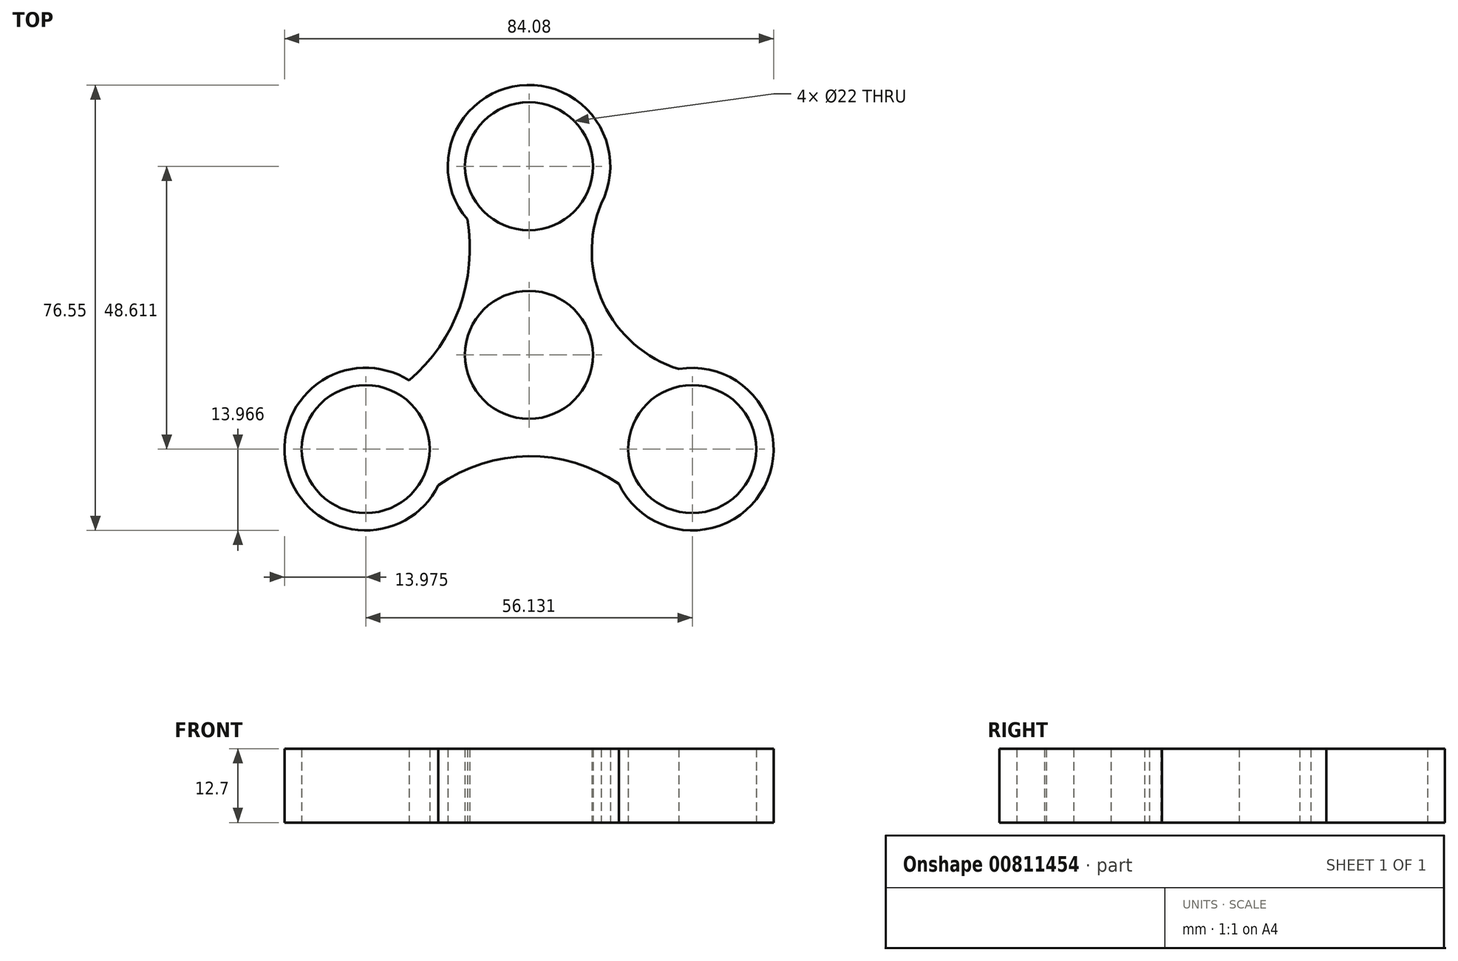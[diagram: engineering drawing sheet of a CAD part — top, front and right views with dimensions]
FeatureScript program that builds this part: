
annotation { "Feature Type Name" : "Feature", "Feature Type Description" : "" }
export const myFeature = defineFeature(function(context is Context, id is Id, definition is map)
    precondition{}
    {
        {
            var Q0;
            Q0=qCreatedBy(makeId("Top.planeOp"),FACE);
            var sketch = newSketch(context, id + "F0", { "sketchPlane" : qUnion([Q0])});
            skCircle(sketch, "E0", {"center": v(0, 0) * mm, "radius": 44.45 * mm});
            skCircle(sketch, "E1", {"center": v(0, 0) * mm, "radius": 11 * mm});
            skCircle(sketch, "E2", {"center": v(0, 32.4) * mm, "radius": 11 * mm});
            skCircle(sketch, "E3.1.0", {"center": v(-28.07, -16.2) * mm, "radius": 11 * mm});
            skCircle(sketch, "E3.2.0", {"center": v(28.07, -16.2) * mm, "radius": 11 * mm});
            skCircle(sketch, "E4", {"center": v(-28.07, -16.2) * mm, "radius": 13.97 * mm});
            skCircle(sketch, "E5", {"center": v(28.07, -16.2) * mm, "radius": 13.97 * mm});
            skCircle(sketch, "E6", {"center": v(0, 32.4) * mm, "radius": 13.97 * mm});
            skCircle(sketch, "E7", {"center": v(0, 0) * mm, "radius": 13.97 * mm});
            skArc(sketch, "E8", {"start": v(-20.59, -4.4) * mm, "mid": v(-11.95, 8.14) * mm, "end": v(-10.6, 23.3) * mm});
            skArc(sketch, "E9", {"start": v(15.42, -22.15) * mm, "mid": v(-0.12, -17.42) * mm, "end": v(-15.57, -22.45) * mm});
            skArc(sketch, "E10", {"start": v(12.4, 25.98) * mm, "mid": v(12.8, 8.83) * mm, "end": v(25.74, -2.43) * mm});
            skSolve(sketch);
        }
        {
            var Q0;
            Q0=makeQuery(id+"F0.imprint","IMPRINT",FACE,{"disambiguationData":[TD([[makeQuery(id+"F0.imprint","IMPRINT",EDGE,{"derivedFrom":sQuery(id+"F0.wireOp",EDGE,"E2")}),-1.0]])]});
            var Q1;
            Q1=makeQuery(id+"F0.imprint","IMPRINT",FACE,{"disambiguationData":[TD([[makeQuery(id+"F0.imprint","IMPRINT",EDGE,{"derivedFrom":sQuery(id+"F0.wireOp",EDGE,"E3.1.0")}),-1.0]])]});
            var Q2;
            {var subQ0=sQuery(id+"F0.wireOp",EDGE,"E4");var subQ1=sQuery(id+"F0.wireOp",EDGE,"E0");var subQ2=makeQuery(id+"F0.imprint","INTERSECT",VERTEX,{"disambiguationData":[OD(0.0)],"derivedFrom":[subQ1,subQ0]});Q2=makeQuery(id+"F0.imprint","IMPRINT",FACE,{"disambiguationData":[TD([[makeQuery(id+"F0.imprint","IMPRINT",EDGE,{"disambiguationData":[TD([[subQ2,-1.0]])],"derivedFrom":subQ1}),-1.0]])]});}
            var Q3;
            {var subQ0=sQuery(id+"F0.wireOp",EDGE,"E6");var subQ1=sQuery(id+"F0.wireOp",EDGE,"E0");var subQ2=makeQuery(id+"F0.imprint","INTERSECT",VERTEX,{"disambiguationData":[OD(0.0)],"derivedFrom":[subQ1,subQ0]});Q3=makeQuery(id+"F0.imprint","IMPRINT",FACE,{"disambiguationData":[TD([[makeQuery(id+"F0.imprint","IMPRINT",EDGE,{"disambiguationData":[TD([[subQ2,1.0]])],"derivedFrom":subQ1}),-1.0]])]});}
            var Q4;
            Q4=makeQuery(id+"F0.imprint","IMPRINT",FACE,{"disambiguationData":[TD([[makeQuery(id+"F0.imprint","IMPRINT",EDGE,{"derivedFrom":sQuery(id+"F0.wireOp",EDGE,"E3.2.0")}),-1.0]])]});
            var Q5;
            {var subQ0=sQuery(id+"F0.wireOp",EDGE,"E5");var subQ1=sQuery(id+"F0.wireOp",EDGE,"E0");var subQ2=makeQuery(id+"F0.imprint","INTERSECT",VERTEX,{"disambiguationData":[OD(0.0)],"derivedFrom":[subQ1,subQ0]});Q5=makeQuery(id+"F0.imprint","IMPRINT",FACE,{"disambiguationData":[TD([[makeQuery(id+"F0.imprint","IMPRINT",EDGE,{"disambiguationData":[TD([[subQ2,-1.0]])],"derivedFrom":subQ1}),-1.0]])]});}
            var Q6;
            Q6=makeQuery(id+"F0.imprint","IMPRINT",FACE,{"disambiguationData":[TD([[makeQuery(id+"F0.imprint","IMPRINT",EDGE,{"derivedFrom":sQuery(id+"F0.wireOp",EDGE,"E1")}),-1.0]])]});
            var Q7;
            Q7=makeQuery(id+"F0.imprint","IMPRINT",FACE,{"disambiguationData":[TD([[makeQuery(id+"F0.imprint","IMPRINT",EDGE,{"derivedFrom":sQuery(id+"F0.wireOp",EDGE,"E7")}),-1.0]])]});
            extrude(context, id + "F1", {"entities" : qUnion([Q0, Q1, Q2, Q3, Q4, Q5, Q6, Q7]), "depth" : 12.7 * mm, "offsetDistance" : 25.4 * mm});
        }
    });
